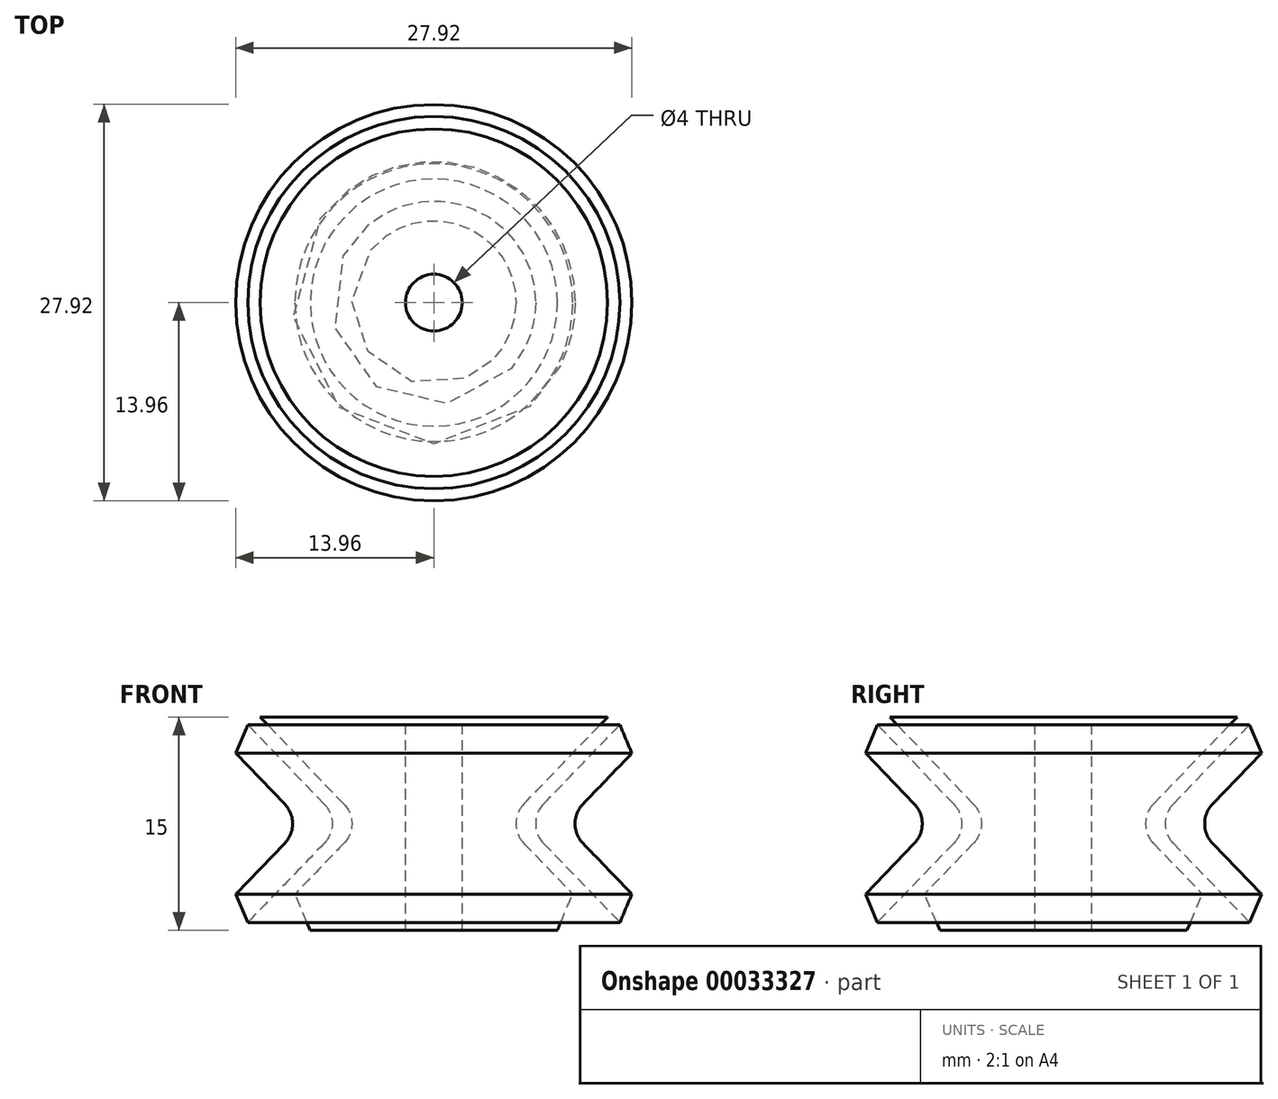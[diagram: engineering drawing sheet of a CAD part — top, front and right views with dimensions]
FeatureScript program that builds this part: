
annotation { "Feature Type Name" : "Feature", "Feature Type Description" : "" }
export const myFeature = defineFeature(function(context is Context, id is Id, definition is map)
    precondition{}
    {
        {
            var Q0;
            Q0=qCreatedBy(makeId("Front.planeOp"),FACE);
            var sketch = newSketch(context, id + "F0", { "sketchPlane" : qUnion([Q0])});
            skLineSegment(sketch, "E0", {"start": v(0, 3.45) * mm, "end": v(0, -3.72) * mm, "construction": true});
            skLineSegment(sketch, "E1", {"start": v(-2, 7.5) * mm, "end": v(-2, -7.5) * mm});
            skLineSegment(sketch, "E2", {"start": v(-2, 7.5) * mm, "end": v(-12.24, 7.5) * mm});
            skLineSegment(sketch, "E3", {"start": v(-2, -7.5) * mm, "end": v(-12.24, -7.5) * mm});
            skLineSegment(sketch, "E4", {"start": v(-12.24, 7.5) * mm, "end": v(-6.34, 1.39) * mm});
            skLineSegment(sketch, "E5", {"start": v(-6.34, -1.39) * mm, "end": v(-12.24, -7.5) * mm});
            skPoint(sketch, "E6", {"position": v(-2, 0) * mm});
            skLineSegment(sketch, "E7", {"start": v(-13.63, 7.5) * mm, "end": v(-7.73, 1.39) * mm});
            skLineSegment(sketch, "E8", {"start": v(-7.73, -1.39) * mm, "end": v(-13.63, -7.5) * mm});
            skCircle(sketch, "E9", {"center": v(-11.95, 0) * mm, "radius": 2 * mm, "construction": true});
            skLineSegment(sketch, "E10", {"start": v(-10.51, 1.39) * mm, "end": v(-16.41, 7.5) * mm});
            skLineSegment(sketch, "E11", {"start": v(-10.51, -1.39) * mm, "end": v(-16.41, -7.5) * mm});
            skArc(sketch, "E12", {"start": v(-10.51, -1.39) * mm, "mid": v(-9.95, 0) * mm, "end": v(-10.51, 1.39) * mm});
            skLineSegment(sketch, "E13", {"start": v(-16.41, 7.5) * mm, "end": v(-13.63, 7.5) * mm});
            skLineSegment(sketch, "E14", {"start": v(-16.41, -7.5) * mm, "end": v(-13.63, -7.5) * mm});
            skLineSegment(sketch, "E15.bottom", {"start": v(-12.24, 7.5) * mm, "end": v(-2, 7.5) * mm});
            skLineSegment(sketch, "E15.top", {"start": v(-12.24, 9.5) * mm, "end": v(-2, 9.5) * mm});
            skLineSegment(sketch, "E15.left", {"start": v(-12.24, 7.5) * mm, "end": v(-12.24, 9.5) * mm});
            skLineSegment(sketch, "E15.right", {"start": v(-2, 7.5) * mm, "end": v(-2, 9.5) * mm});
            skPoint(sketch, "E16.visualSharp", {"position": v(-6.4, 0) * mm});
            skArc(sketch, "E16.filletArc", {"start": v(-7.73, -1.39) * mm, "mid": v(-7.17, 0) * mm, "end": v(-7.73, 1.39) * mm});
            skPoint(sketch, "E17.visualSharp", {"position": v(-5, 0) * mm});
            skArc(sketch, "E17.filletArc", {"start": v(-6.34, -1.39) * mm, "mid": v(-5.78, 0) * mm, "end": v(-6.34, 1.39) * mm});
            skSolve(sketch);
        }
        {
            var Q0;
            Q0=makeQuery(id+"F0.imprint","IMPRINT",FACE,{"disambiguationData":[TD([[makeQuery(id+"F0.imprint","IMPRINT",EDGE,{"derivedFrom":sQuery(id+"F0.wireOp",EDGE,"E1")}),-1.0]])]});
            var Q1;
            Q1=makeQuery(id+"F0.imprint","IMPRINT",FACE,{"disambiguationData":[TD([[makeQuery(id+"F0.imprint","IMPRINT",EDGE,{"derivedFrom":sQuery(id+"F0.wireOp",EDGE,"E15.bottom")}),1.0]])]});
            var Q2;
            Q2=makeQuery(id+"F0.imprint","IMPRINT",FACE,{"disambiguationData":[TD([[makeQuery(id+"F0.imprint","IMPRINT",EDGE,{"derivedFrom":sQuery(id+"F0.wireOp",EDGE,"E7")}),-1.0]])]});
            var Q3;
            Q3=sQuery(id+"F0.wireOp",EDGE,"E0");
            revolve(context, id + "F1", {"entities" : qUnion([Q0, Q1, Q2]), "axis" : qUnion([Q3]), "revolveType" : RevolveType.FULL});
        }
        {
            var Q0;
            Q0=makeQuery(id+"F1.opRevolve","SWEPT_EDGE",EDGE,{"disambiguationData":[OSD([sQuery(id+"F0.wireOp",EDGE,"E3"),sQuery(id+"F0.wireOp",EDGE,"E5")])]});
            var Q1;
            Q1=makeQuery(id+"F1.opRevolve","SWEPT_EDGE",EDGE,{"disambiguationData":[OSD([sQuery(id+"F0.wireOp",EDGE,"E11"),sQuery(id+"F0.wireOp",EDGE,"E14")])]});
            var Q2;
            Q2=makeQuery(id+"F1.opRevolve","SWEPT_EDGE",EDGE,{"disambiguationData":[OSD([sQuery(id+"F0.wireOp",EDGE,"E10"),sQuery(id+"F0.wireOp",EDGE,"E13")])]});
            chamfer(context, id + "F2", {"entities" : qUnion([Q0, Q1, Q2]), "width" : 1.5 * mm, "tangentPropagation" : true});
        }
    });
